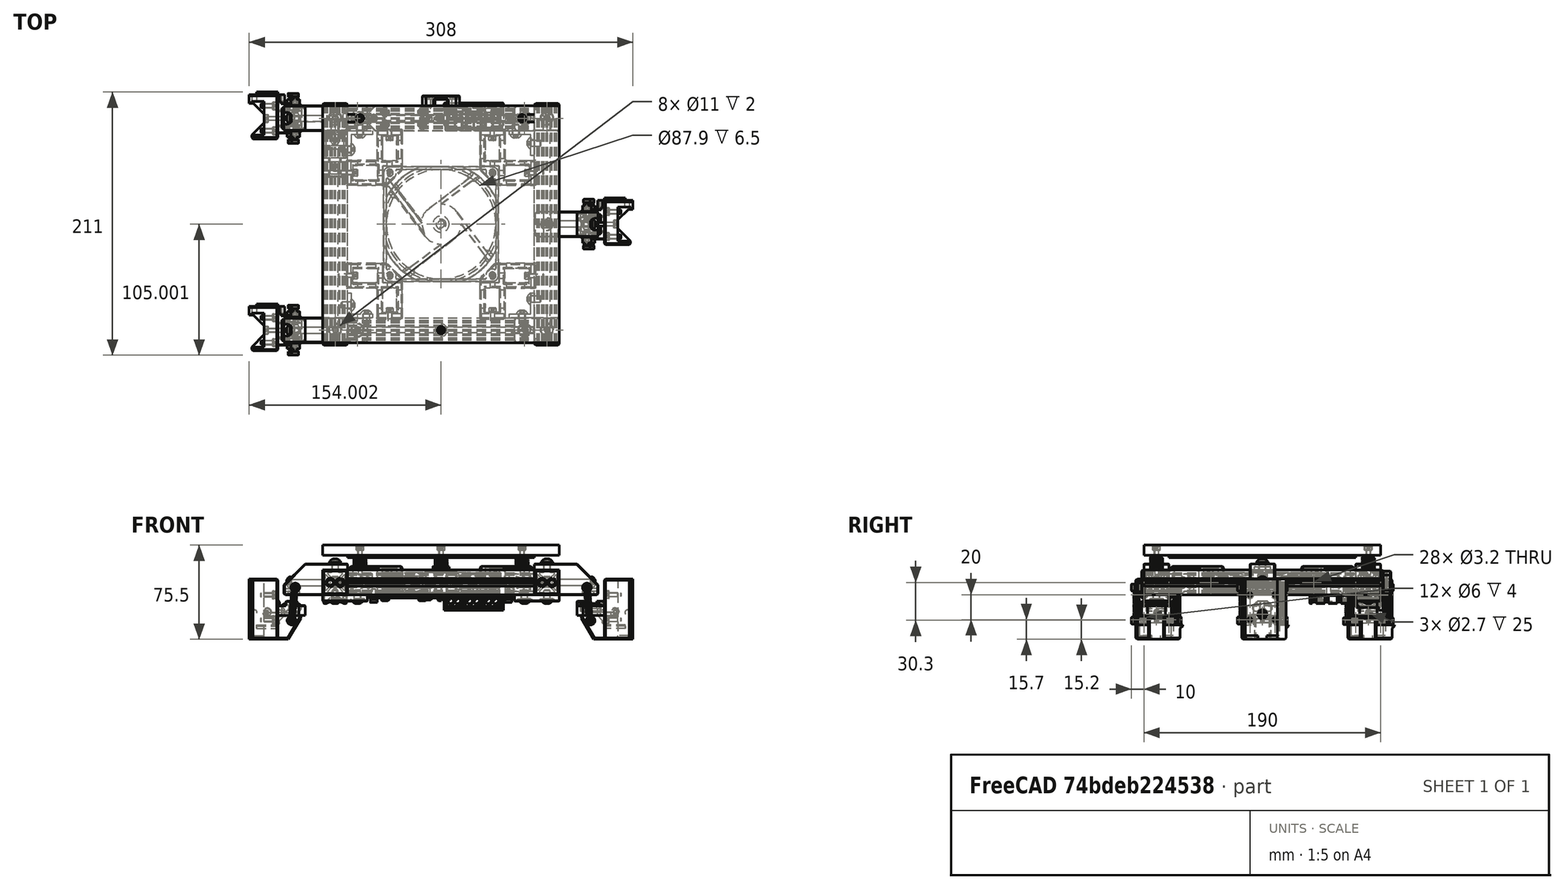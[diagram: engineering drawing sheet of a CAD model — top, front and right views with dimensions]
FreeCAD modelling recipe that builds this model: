
FCSTD DOCUMENT  (FreeCAD 0.19R24291 (Git))
Label: 180-bed-assembly
License: Other
LicenseURL: GPL3
objects: Part::FeaturePython×107, Part::Feature×58, App::Part×6, Part::Cylinder×6, Part::Sphere×3, Part::Box×1
note: 175 computed .brp shape members not serialized (recipe doc carries the construction recipe); baked Part::Feature solids carry a one-line shape summary decoded from their .brp

FEATURE [Part::Feature] Extrude003001  label="2020-190mm001"
  Placement = pos=(-85,-95,2.1e-14) rot=(-1,0,0;1.5708rad)
  shape: bbox 20 x 190 x 20 mm, 63 faces (baked)
FEATURE [Part::Feature] Extrude002  label="2020-150mm001"
  Placement = pos=(-75,-85,-1.7e-14) rot=(0,1,0;1.5708rad)
  shape: bbox 150 x 20 x 20 mm, 63 faces (baked)
FEATURE [Part::Feature] Extrude003002  label="2020-190mm002"
  Placement = pos=(85,-95,2.1e-14) rot=(-1,0,0;1.5708rad)
  shape: bbox 20 x 190 x 20 mm, 63 faces (baked)
FEATURE [Part::Feature] Extrude003003  label="2020-150mm002"
  Placement = pos=(-75,85,-1.7e-14) rot=(0,1,0;1.5708rad)
  shape: bbox 150 x 20 x 20 mm, 63 faces (baked)
FEATURE [Part::Box] Box001  label="150mm-heater-pad"
  AttacherType = Attacher::AttachEngine3D
  Height = 2
  Length = 150
  Placement = pos=(-75,-75,20) rot=(0,0,1;0rad)
  Width = 150
FEATURE [Part::Feature] AdditivePipe001  label="15mm-spring001"
  Placement = pos=(65,85,10) rot=(0,0,1;0rad)
  shape: bbox 10.45 x 11.2 x 10.36 mm, 42 faces (baked)
FEATURE [Part::Feature] AdditivePipe003  label="15mm-spring002"
  Placement = pos=(0,-85,10) rot=(0,0,1;0rad)
  shape: bbox 10.45 x 11.2 x 10.36 mm, 42 faces (baked)
FEATURE [Part::Feature] AdditivePipe005  label="15mm-spring003"
  Placement = pos=(-65,85,10) rot=(0,0,1;0rad)
  shape: bbox 10.45 x 11.2 x 10.36 mm, 42 faces (baked)
FEATURE [Part::Sphere] Sphere  label="8mm-ball-bearing"
  Angle1 = -90
  Angle2 = 90
  Angle3 = 360
  AttacherType = Attacher::AttachEngine3D
  Placement = pos=(0,0,4.9) rot=(0,0,1;0rad)
  Radius = 4
FEATURE [Part::Sphere] Sphere001  label="8mm-ball-bearing001"
  Angle1 = -90
  Angle2 = 90
  Angle3 = 360
  AttacherType = Attacher::AttachEngine3D
  Placement = pos=(0,0,4.9) rot=(0,0,1;0rad)
  Radius = 4
FEATURE [Part::Sphere] Sphere002  label="8mm-ball-bearing002"
  Angle1 = -90
  Angle2 = 90
  Angle3 = 360
  AttacherType = Attacher::AttachEngine3D
  Placement = pos=(0,0,4.9) rot=(0,0,1;0rad)
  Radius = 4
FEATURE [App::Part] Part005  label="bed-frame"
  Group = -> [Extrude003001,Extrude002,Extrude003002,Extrude003003]
  Origin = -> Origin005
FEATURE [Part::Feature] Cut010  label="190-aluminum-bed"
  shape: bbox 190 x 190 x 8 mm, 15 faces (baked)
FEATURE [Part::Feature] Cut007001  label="13x5.5x5-magnet003"
  shape: bbox 13 x 13 x 5 mm, 4 faces (baked)
FEATURE [App::Part] Part002  label="bed-magnet-slider002"
  Group = -> [Sphere002,Cut007001]
  Origin = -> Origin002
  Placement = pos=(-120,-85,-20) rot=(0,0,1;0rad)
FEATURE [Part::Feature] Cut003001  label="13x5.5x5-magnet004"
  shape: bbox 13 x 13 x 5 mm, 4 faces (baked)
FEATURE [App::Part] Part  label="bed-magnet-slider003"
  Group = -> [Sphere,Cut003001]
  Origin = -> Origin
  Placement = pos=(120,0,-20) rot=(0,0,1;1.5708rad)
FEATURE [Part::Feature] Cut006001  label="13x5.5x5-magnet005"
  shape: bbox 13 x 13 x 5 mm, 4 faces (baked)
FEATURE [App::Part] Part001  label="bed-magnet-slider001"
  Group = -> [Sphere001,Cut006001]
  Origin = -> Origin001
  Placement = pos=(-120,85,-20) rot=(0,0,1;0rad)
FEATURE [App::Part] Part006  label="bed-magnet"
  Group = -> [Part,Part001,Part002]
  Origin = -> Origin006
FEATURE [Part::Feature] Solid  label="2020-bracket"
  Placement = pos=(-75,-75,-1.7e-14) rot=(0,1,0;1.5708rad)
  shape: bbox 20 x 20 x 14 mm, 10 faces (baked)
FEATURE [Part::Feature] Solid001  label="2020-bracket001"
  Placement = pos=(75,-75,1.6e-14) rot=(0.57735,-0.57735,-0.57735;4.18879rad)
  shape: bbox 20 x 20 x 14 mm, 10 faces (baked)
FEATURE [Part::Feature] Solid002  label="2020-bracket002"
  Placement = pos=(75,75,1.6e-14) rot=(0.707107,0,-0.707107;3.14159rad)
  shape: bbox 20 x 20 x 14 mm, 10 faces (baked)
FEATURE [Part::Feature] Solid003  label="2020-bracket003"
  Placement = pos=(-75,75,-1.7e-14) rot=(0.57735,0.57735,-0.57735;2.0944rad)
  shape: bbox 20 x 20 x 14 mm, 10 faces (baked)
FEATURE [Part::FeaturePython] Screw  label="M5x8-Screw"  # Fasteners workbench fastener (typed FeaturePython)
  Placement = pos=(-72,-65,-1.6e-14) rot=(0,1,0;1.5708rad)
  baseObject = -> Solid [Edge1]
  diameter = 3
  invert = false
  length = 0
  lengthCustom = 8
  matchOuter = true
  offset = 0
  thread = false
  type = 39
FEATURE [Part::FeaturePython] Screw001  label="M5x8-Screw001"  # Fasteners workbench fastener (typed FeaturePython)
  Placement = pos=(-60,-72,-1.42e-14) rot=(-1,0,0;1.5708rad)
  baseObject = -> Solid [Edge13]
  diameter = 3
  invert = false
  length = 0
  lengthCustom = 8
  matchOuter = true
  offset = 0
  thread = false
  type = 39
FEATURE [Part::FeaturePython] Screw002  label="M5x8-Screw002"  # Fasteners workbench fastener (typed FeaturePython)
  Placement = pos=(65,-72,1.4e-14) rot=(-1,0,0;1.5708rad)
  baseObject = -> Solid001 [Edge1]
  diameter = 3
  invert = false
  length = 0
  lengthCustom = 8
  matchOuter = true
  offset = 0
  thread = false
  type = 39
FEATURE [Part::FeaturePython] Screw003  label="M5x8-Screw003"  # Fasteners workbench fastener (typed FeaturePython)
  Placement = pos=(72,-60,1.5e-14) rot=(0,-1,0;1.5708rad)
  baseObject = -> Solid001 [Edge13]
  diameter = 3
  invert = false
  length = 0
  lengthCustom = 8
  matchOuter = true
  offset = 0
  thread = false
  type = 39
FEATURE [Part::FeaturePython] Screw004  label="M5x8-Screw004"  # Fasteners workbench fastener (typed FeaturePython)
  Placement = pos=(72,65,1.7e-14) rot=(0,-1,0;1.5708rad)
  baseObject = -> Solid002 [Edge1]
  diameter = 3
  invert = false
  length = 0
  lengthCustom = 8
  matchOuter = true
  offset = 0
  thread = false
  type = 39
FEATURE [Part::FeaturePython] Screw005  label="M5x8-Screw005"  # Fasteners workbench fastener (typed FeaturePython)
  Placement = pos=(60,72,1.8e-14) rot=(1,0,0;1.5708rad)
  baseObject = -> Solid002 [Edge13]
  diameter = 3
  invert = false
  length = 0
  lengthCustom = 8
  matchOuter = true
  offset = 0
  thread = false
  type = 39
FEATURE [Part::FeaturePython] Screw006  label="M5x8-Screw006"  # Fasteners workbench fastener (typed FeaturePython)
  Placement = pos=(-72,60,-1.8e-14) rot=(0,1,0;1.5708rad)
  baseObject = -> Solid003 [Edge13]
  diameter = 3
  invert = false
  length = 0
  lengthCustom = 8
  matchOuter = true
  offset = 0
  thread = false
  type = 39
FEATURE [Part::FeaturePython] Screw007  label="M5x8-Screw007"  # Fasteners workbench fastener (typed FeaturePython)
  Placement = pos=(-65,72,-1.5e-14) rot=(1,0,0;1.5708rad)
  baseObject = -> Solid003 [Edge1]
  diameter = 3
  invert = false
  length = 0
  lengthCustom = 8
  matchOuter = true
  offset = 0
  thread = false
  type = 39
FEATURE [Part::FeaturePython] Screw011  label="M3x20-Screw"  # Fasteners workbench fastener (typed FeaturePython)
  Placement = pos=(0,-85,26) rot=(0,0,1;0rad)
  baseObject = -> Cut010 [Edge25]
  diameter = 4
  invert = false
  length = 10
  lengthCustom = 20
  matchOuter = true
  offset = 0
  thread = false
  type = 33
FEATURE [Part::FeaturePython] Screw012  label="M3x20-Screw001"  # Fasteners workbench fastener (typed FeaturePython)
  Placement = pos=(65,85,26) rot=(0,0,1;0rad)
  baseObject = -> Cut010 [Edge29]
  diameter = 4
  invert = false
  length = 10
  lengthCustom = 20
  matchOuter = true
  offset = 0
  thread = false
  type = 33
FEATURE [Part::FeaturePython] Screw013  label="M3x20-Screw002"  # Fasteners workbench fastener (typed FeaturePython)
  Placement = pos=(-65,85,26) rot=(0,0,1;0rad)
  baseObject = -> Cut010 [Edge27]
  diameter = 4
  invert = false
  length = 10
  lengthCustom = 20
  matchOuter = true
  offset = 0
  thread = false
  type = 33
FEATURE [Part::FeaturePython] Washer010  label="M3-Washer"  # Fasteners workbench fastener (typed FeaturePython)
  Placement = pos=(-135,-95,-29.8) rot=(0,1,0;1.5708rad)
  diameter = 4
  invert = false
  matchOuter = true
  offset = 0
  type = 5
FEATURE [Part::FeaturePython] Washer011  label="M3-Washer042"  # Fasteners workbench fastener (typed FeaturePython)
  Placement = pos=(-135,-95,-9.8) rot=(0,1,0;1.5708rad)
  diameter = 4
  invert = false
  matchOuter = true
  offset = 0
  type = 5
FEATURE [Part::FeaturePython] Washer012  label="M3-Washer043"  # Fasteners workbench fastener (typed FeaturePython)
  Placement = pos=(-135,-75,-9.8) rot=(0,1,0;1.5708rad)
  diameter = 4
  invert = false
  matchOuter = true
  offset = 0
  type = 5
FEATURE [Part::FeaturePython] Washer013  label="M3-Washer041"  # Fasteners workbench fastener (typed FeaturePython)
  Placement = pos=(-135,-75,-29.8) rot=(0,1,0;1.5708rad)
  diameter = 4
  invert = false
  matchOuter = true
  offset = 0
  type = 5
FEATURE [Part::FeaturePython] Washer014  label="M3-Washer046"  # Fasteners workbench fastener (typed FeaturePython)
  Placement = pos=(-135,75,-30.3) rot=(0,1,0;1.5708rad)
  diameter = 4
  invert = false
  matchOuter = true
  offset = 0
  type = 5
FEATURE [Part::FeaturePython] Washer015  label="M3-Washer047"  # Fasteners workbench fastener (typed FeaturePython)
  Placement = pos=(-135,75,-10.3) rot=(0,1,0;1.5708rad)
  diameter = 4
  invert = false
  matchOuter = true
  offset = 0
  type = 5
FEATURE [Part::FeaturePython] Washer016  label="M3-Washer045"  # Fasteners workbench fastener (typed FeaturePython)
  Placement = pos=(-135,95,-10.3) rot=(0,1,0;1.5708rad)
  diameter = 4
  invert = false
  matchOuter = true
  offset = 0
  type = 5
FEATURE [Part::FeaturePython] Washer017  label="M3-Washer044"  # Fasteners workbench fastener (typed FeaturePython)
  Placement = pos=(-135,95,-30.3) rot=(0,1,0;1.5708rad)
  diameter = 4
  invert = false
  matchOuter = true
  offset = 0
  type = 5
FEATURE [Part::FeaturePython] Screw034  label="M3x10-Screw044"  # Fasteners workbench fastener (typed FeaturePython)
  Placement = pos=(-134.45,75,-10.3) rot=(0,1,0;1.5708rad)
  baseObject = -> Washer015 [Edge1]
  diameter = 4
  invert = false
  length = 3
  lengthCustom = 10
  matchOuter = true
  offset = 0
  thread = false
  type = 33
FEATURE [Part::FeaturePython] Screw035  label="M3x10-Screw043"  # Fasteners workbench fastener (typed FeaturePython)
  Placement = pos=(-134.45,95,-10.3) rot=(0,1,0;1.5708rad)
  baseObject = -> Washer016 [Edge1]
  diameter = 4
  invert = false
  length = 3
  lengthCustom = 10
  matchOuter = true
  offset = 0
  thread = false
  type = 33
FEATURE [Part::FeaturePython] Screw036  label="M3x10-Screw042"  # Fasteners workbench fastener (typed FeaturePython)
  Placement = pos=(-134.45,95,-30.3) rot=(0,1,0;1.5708rad)
  baseObject = -> Washer017 [Edge1]
  diameter = 4
  invert = false
  length = 3
  lengthCustom = 10
  matchOuter = true
  offset = 0
  thread = false
  type = 33
FEATURE [Part::FeaturePython] Screw037  label="M3x10-Screw041"  # Fasteners workbench fastener (typed FeaturePython)
  Placement = pos=(-134.45,75,-30.3) rot=(0,1,0;1.5708rad)
  baseObject = -> Washer014 [Edge1]
  diameter = 4
  invert = false
  length = 3
  lengthCustom = 10
  matchOuter = true
  offset = 0
  thread = false
  type = 33
FEATURE [Part::FeaturePython] Screw039  label="M3x10-Screw038"  # Fasteners workbench fastener (typed FeaturePython)
  Placement = pos=(-134.45,-95,-29.8) rot=(0,1,0;1.5708rad)
  baseObject = -> Washer010 [Edge1]
  diameter = 4
  invert = false
  length = 3
  lengthCustom = 10
  matchOuter = true
  offset = 0
  thread = false
  type = 33
FEATURE [Part::FeaturePython] Screw040  label="M3x10-Screw037"  # Fasteners workbench fastener (typed FeaturePython)
  Placement = pos=(-134.45,-75,-29.8) rot=(0,1,0;1.5708rad)
  baseObject = -> Washer013 [Edge1]
  diameter = 4
  invert = false
  length = 3
  lengthCustom = 10
  matchOuter = true
  offset = 0
  thread = false
  type = 33
FEATURE [Part::FeaturePython] Screw041  label="M3x10-Screw040"  # Fasteners workbench fastener (typed FeaturePython)
  Placement = pos=(-134.45,-75,-9.8) rot=(0,1,0;1.5708rad)
  baseObject = -> Washer012 [Edge1]
  diameter = 4
  invert = false
  length = 3
  lengthCustom = 10
  matchOuter = true
  offset = 0
  thread = false
  type = 33
FEATURE [Part::FeaturePython] Screw042  label="M3x10-Screw039"  # Fasteners workbench fastener (typed FeaturePython)
  Placement = pos=(-134.45,-95,-9.8) rot=(0,1,0;1.5708rad)
  baseObject = -> Washer011 [Edge1]
  diameter = 4
  invert = false
  length = 3
  lengthCustom = 10
  matchOuter = true
  offset = 0
  thread = false
  type = 33
FEATURE [Part::FeaturePython] Washer018  label="M3-Washer049"  # Fasteners workbench fastener (typed FeaturePython)
  Placement = pos=(135,10,-9.8) rot=(0,-1,0;1.5708rad)
  diameter = 4
  invert = true
  matchOuter = true
  offset = 0
  type = 5
FEATURE [Part::FeaturePython] Washer019  label="M3-Washer050"  # Fasteners workbench fastener (typed FeaturePython)
  Placement = pos=(135,10,-29.8) rot=(0,-1,0;1.5708rad)
  diameter = 4
  invert = true
  matchOuter = true
  offset = 0
  type = 5
FEATURE [Part::FeaturePython] Washer020  label="M3-Washer048"  # Fasteners workbench fastener (typed FeaturePython)
  Placement = pos=(135,-10,-9.8) rot=(0,-1,0;1.5708rad)
  diameter = 4
  invert = true
  matchOuter = true
  offset = 0
  type = 5
FEATURE [Part::FeaturePython] Washer021  label="M3-Washer051"  # Fasteners workbench fastener (typed FeaturePython)
  Placement = pos=(135,-10,-29.8) rot=(0,-1,0;1.5708rad)
  diameter = 4
  invert = true
  matchOuter = true
  offset = 0
  type = 5
FEATURE [Part::FeaturePython] Screw043  label="M3x10-Screw046"  # Fasteners workbench fastener (typed FeaturePython)
  Placement = pos=(134.45,10,-29.8) rot=(0,-1,0;1.5708rad)
  baseObject = -> Washer019 [Edge1]
  diameter = 4
  invert = false
  length = 10
  lengthCustom = 10
  matchOuter = true
  offset = 0
  thread = false
  type = 33
FEATURE [Part::FeaturePython] Screw044  label="M3x10-Screw047"  # Fasteners workbench fastener (typed FeaturePython)
  Placement = pos=(134.45,-10,-29.8) rot=(0,-1,0;1.5708rad)
  baseObject = -> Washer021 [Edge1]
  diameter = 4
  invert = false
  length = 10
  lengthCustom = 10
  matchOuter = true
  offset = 0
  thread = false
  type = 33
FEATURE [Part::FeaturePython] Screw045  label="M3x10-Screw048"  # Fasteners workbench fastener (typed FeaturePython)
  Placement = pos=(134.45,-10,-9.8) rot=(0,-1,0;1.5708rad)
  baseObject = -> Washer020 [Edge1]
  diameter = 4
  invert = false
  length = 10
  lengthCustom = 10
  matchOuter = true
  offset = 0
  thread = false
  type = 33
FEATURE [Part::FeaturePython] Screw046  label="M3x10-Screw045"  # Fasteners workbench fastener (typed FeaturePython)
  Placement = pos=(134.45,10,-9.8) rot=(0,-1,0;1.5708rad)
  baseObject = -> Washer018 [Edge1]
  diameter = 4
  invert = false
  length = 10
  lengthCustom = 10
  matchOuter = true
  offset = 0
  thread = false
  type = 33
FEATURE [Part::Feature] Chamfer004013007011015006009007001002  label="bed-frame-mount-top005"
  Placement = pos=(-142,85,-45) rot=(0,0,1;0rad)
  shape: bbox 51 x 20 x 25 mm, 56 faces (baked)
FEATURE [Part::Feature] Chamfer004013007011015006009007001003  label="bed-frame-mount-top006"
  Placement = pos=(142,-2.9e-14,-45) rot=(0,0,1;3.14159rad)
  shape: bbox 51 x 20 x 25 mm, 56 faces (baked)
FEATURE [Part::Feature] Chamfer004013007011015006009007001001  label="bed-frame-mount-top004"
  Placement = pos=(-142,-85,-45) rot=(0,0,1;0rad)
  shape: bbox 51 x 20 x 25 mm, 56 faces (baked)
FEATURE [Part::FeaturePython] Screw047  label="M3x12-Screw015"  # Fasteners workbench fastener (typed FeaturePython)
  Placement = pos=(-117,102,-4) rot=(-1,0,0;1.5708rad)
  baseObject = -> Chamfer004013007011015006009007001002 [Edge138]
  diameter = 4
  invert = true
  length = 4
  lengthCustom = 12
  matchOuter = false
  offset = 7
  thread = false
  type = 33
FEATURE [Part::FeaturePython] Screw048  label="M3x12-Screw014"  # Fasteners workbench fastener (typed FeaturePython)
  Placement = pos=(-117,68,-4) rot=(1,0,0;1.5708rad)
  baseObject = -> Chamfer004013007011015006009007001002 [Edge132]
  diameter = 4
  invert = false
  length = 4
  lengthCustom = 12
  matchOuter = false
  offset = 7
  thread = false
  type = 33
FEATURE [Part::FeaturePython] Screw049  label="M3x12-Screw017"  # Fasteners workbench fastener (typed FeaturePython)
  Placement = pos=(-117,-68,-4) rot=(-1,0,0;1.5708rad)
  baseObject = -> Chamfer004013007011015006009007001001 [Edge138]
  diameter = 4
  invert = true
  length = 4
  lengthCustom = 12
  matchOuter = false
  offset = 7
  thread = false
  type = 33
FEATURE [Part::FeaturePython] Screw050  label="M3x12-Screw016"  # Fasteners workbench fastener (typed FeaturePython)
  Placement = pos=(-117,-102,-4) rot=(1,0,0;1.5708rad)
  baseObject = -> Chamfer004013007011015006009007001001 [Edge132]
  diameter = 4
  invert = false
  length = 4
  lengthCustom = 12
  matchOuter = false
  offset = 7
  thread = false
  type = 33
FEATURE [Part::FeaturePython] Screw051  label="M3x12-Screw009"  # Fasteners workbench fastener (typed FeaturePython)
  Placement = pos=(117,-17,-4) rot=(1,0,0;1.5708rad)
  baseObject = -> Chamfer004013007011015006009007001003 [Edge138]
  diameter = 4
  invert = true
  length = 4
  lengthCustom = 12
  matchOuter = true
  offset = 7
  thread = false
  type = 33
FEATURE [Part::FeaturePython] Screw052  label="M3x12-Screw008"  # Fasteners workbench fastener (typed FeaturePython)
  Placement = pos=(117,17,-4) rot=(-1,0,0;1.5708rad)
  baseObject = -> Chamfer004013007011015006009007001003 [Edge132]
  diameter = 4
  invert = false
  length = 4
  lengthCustom = 12
  matchOuter = true
  offset = 7
  thread = false
  type = 33
FEATURE [Part::FeaturePython] Washer  label="M5-Washer"  # Fasteners workbench fastener (typed FeaturePython)
  Placement = pos=(-85,85,15) rot=(0,0,1;0rad)
  baseObject = -> Chamfer004013007011015006009007001002 [Edge58]
  diameter = 1
  invert = false
  matchOuter = true
  offset = 0
  type = 4
FEATURE [Part::FeaturePython] Washer022  label="M5-Washer001"  # Fasteners workbench fastener (typed FeaturePython)
  Placement = pos=(-85,-85,15) rot=(0,0,1;0rad)
  baseObject = -> Chamfer004013007011015006009007001001 [Edge58]
  diameter = 1
  invert = false
  matchOuter = true
  offset = 0
  type = 4
FEATURE [Part::FeaturePython] Washer023  label="M5-Washer002"  # Fasteners workbench fastener (typed FeaturePython)
  Placement = pos=(85,-2.19e-14,15) rot=(0,0,1;0rad)
  baseObject = -> Chamfer004013007011015006009007001003 [Edge58]
  diameter = 1
  invert = false
  matchOuter = true
  offset = 0
  type = 4
FEATURE [Part::FeaturePython] Screw053  label="M5x12-Screw"  # Fasteners workbench fastener (typed FeaturePython)
  Placement = pos=(-85,85,16.1) rot=(0,0,1;0rad)
  baseObject = -> Washer [Edge1]
  diameter = 3
  invert = false
  length = 2
  lengthCustom = 12
  matchOuter = true
  offset = 0
  thread = false
  type = 39
FEATURE [Part::FeaturePython] Screw054  label="M5x12-Screw001"  # Fasteners workbench fastener (typed FeaturePython)
  Placement = pos=(-85,-85,16.1) rot=(0,0,1;0rad)
  baseObject = -> Washer022 [Edge1]
  diameter = 3
  invert = false
  length = 2
  lengthCustom = 12
  matchOuter = true
  offset = 0
  thread = false
  type = 39
FEATURE [Part::FeaturePython] Screw055  label="M5x12-Screw002"  # Fasteners workbench fastener (typed FeaturePython)
  Placement = pos=(85,-2.19e-14,16.1) rot=(0,0,1;0rad)
  baseObject = -> Washer023 [Edge1]
  diameter = 3
  invert = false
  length = 2
  lengthCustom = 12
  matchOuter = true
  offset = 0
  thread = false
  type = 39
FEATURE [Part::FeaturePython] Washer024  label="M5-Washer006"  # Fasteners workbench fastener (typed FeaturePython)
  Placement = pos=(-120,85,0) rot=(0,-1,0;1.5708rad)
  baseObject = -> Chamfer004013007011015006009007001002 [Edge86]
  diameter = 6
  invert = true
  matchOuter = true
  offset = 0
  type = 5
FEATURE [Part::FeaturePython] Washer025  label="M5-Washer007"  # Fasteners workbench fastener (typed FeaturePython)
  Placement = pos=(-120,-85,0) rot=(0,-1,0;1.5708rad)
  baseObject = -> Chamfer004013007011015006009007001001 [Edge86]
  diameter = 6
  invert = true
  matchOuter = true
  offset = 0
  type = 5
FEATURE [Part::FeaturePython] Washer026  label="M5-Washer005"  # Fasteners workbench fastener (typed FeaturePython)
  Placement = pos=(120,-2.6e-14,0) rot=(0,1,0;1.5708rad)
  baseObject = -> Chamfer004013007011015006009007001003 [Edge86]
  diameter = 6
  invert = true
  matchOuter = true
  offset = 0
  type = 5
FEATURE [Part::FeaturePython] Screw056  label="M5x30-Screw"  # Fasteners workbench fastener (typed FeaturePython)
  Placement = pos=(-121.1,85,0) rot=(0,-1,0;1.5708rad)
  baseObject = -> Washer024 [Edge1]
  diameter = 3
  invert = false
  length = 7
  lengthCustom = 30
  matchOuter = true
  offset = 0
  thread = false
  type = 39
FEATURE [Part::FeaturePython] Screw057  label="M5x30-Screw001"  # Fasteners workbench fastener (typed FeaturePython)
  Placement = pos=(-121.1,-85,0) rot=(0,-1,0;1.5708rad)
  baseObject = -> Washer025 [Edge1]
  diameter = 3
  invert = false
  length = 7
  lengthCustom = 30
  matchOuter = true
  offset = 0
  thread = false
  type = 39
FEATURE [Part::FeaturePython] Screw058  label="M5x30-Screw002"  # Fasteners workbench fastener (typed FeaturePython)
  Placement = pos=(121.1,-2.6e-14,0) rot=(0,1,0;1.5708rad)
  baseObject = -> Washer026 [Edge1]
  diameter = 3
  invert = false
  length = 7
  lengthCustom = 30
  matchOuter = true
  offset = 0
  thread = false
  type = 39
FEATURE [Part::FeaturePython] Screw059  label="M3x16-Screw007"  # Fasteners workbench fastener (typed FeaturePython)
  Placement = pos=(-120,-102,-30.5) rot=(1,0,0;1.5708rad)
  diameter = 4
  invert = false
  length = 6
  lengthCustom = 16
  matchOuter = true
  offset = 6.5
  thread = false
  type = 33
FEATURE [Part::FeaturePython] Screw060  label="M3x16-Screw"  # Fasteners workbench fastener (typed FeaturePython)
  Placement = pos=(-120,-68,-30.5) rot=(-1,0,0;1.5708rad)
  diameter = 4
  invert = true
  length = 6
  lengthCustom = 16
  matchOuter = true
  offset = 6.5
  thread = false
  type = 33
FEATURE [Part::FeaturePython] Screw061  label="M3x16-Screw009"  # Fasteners workbench fastener (typed FeaturePython)
  Placement = pos=(-120,102,-31) rot=(-1,0,0;1.5708rad)
  diameter = 4
  invert = true
  length = 6
  lengthCustom = 16
  matchOuter = true
  offset = 6.5
  thread = false
  type = 33
FEATURE [Part::FeaturePython] Screw062  label="M3x16-Screw008"  # Fasteners workbench fastener (typed FeaturePython)
  Placement = pos=(-120,68,-31) rot=(1,0,0;1.5708rad)
  diameter = 4
  invert = false
  length = 6
  lengthCustom = 16
  matchOuter = true
  offset = 6.5
  thread = false
  type = 33
FEATURE [Part::FeaturePython] Screw063  label="M3x16-Screw005"  # Fasteners workbench fastener (typed FeaturePython)
  Placement = pos=(120,-17,-30.5) rot=(1,0,0;1.5708rad)
  diameter = 4
  invert = true
  length = 6
  lengthCustom = 16
  matchOuter = true
  offset = 6.5
  thread = false
  type = 33
FEATURE [Part::FeaturePython] Screw064  label="M3x16-Screw006"  # Fasteners workbench fastener (typed FeaturePython)
  Placement = pos=(120,17,-30.5) rot=(-1,0,0;1.5708rad)
  diameter = 4
  invert = false
  length = 6
  lengthCustom = 16
  matchOuter = true
  offset = 6.5
  thread = false
  type = 33
FEATURE [Part::Feature] Chamfer001
  Placement = pos=(-95,-95,-15) rot=(0,0,1;0rad)
  shape: bbox 36 x 20 x 6 mm, 35 faces (baked)
FEATURE [Part::Feature] Chamfer004013007011015006009007001005
  Placement = pos=(95,95,-15) rot=(0,0,1;3.14159rad)
  shape: bbox 36 x 20 x 6 mm, 35 faces (baked)
FEATURE [Part::Feature] Chamfer004013007011015006009007001006
  Placement = pos=(95,-75,-15) rot=(0,0,1;3.14159rad)
  shape: bbox 36 x 20 x 6 mm, 35 faces (baked)
FEATURE [Part::FeaturePython] Washer027  label="M5-Washer016"  # Fasteners workbench fastener (typed FeaturePython)
  Placement = pos=(-85,-85,-13) rot=(1,0,0;3.14159rad)
  baseObject = -> Chamfer001 [Edge75]
  diameter = 1
  invert = true
  matchOuter = true
  offset = 0
  type = 4
FEATURE [Part::FeaturePython] Washer028  label="M5-Washer017"  # Fasteners workbench fastener (typed FeaturePython)
  Placement = pos=(-67,-85,-13) rot=(1,0,0;3.14159rad)
  baseObject = -> Chamfer001 [Edge74]
  diameter = 1
  invert = true
  matchOuter = true
  offset = 0
  type = 4
FEATURE [Part::FeaturePython] Washer029  label="M5-Washer025"  # Fasteners workbench fastener (typed FeaturePython)
  Placement = pos=(-85,85,-13) rot=(1,0,0;3.14159rad)
  diameter = 1
  invert = true
  matchOuter = true
  offset = 0
  type = 4
FEATURE [Part::FeaturePython] Washer030  label="M5-Washer024"  # Fasteners workbench fastener (typed FeaturePython)
  Placement = pos=(-67,85,-13) rot=(1,0,0;3.14159rad)
  diameter = 1
  invert = true
  matchOuter = true
  offset = 0
  type = 4
FEATURE [Part::FeaturePython] Washer031  label="M5-Washer020"  # Fasteners workbench fastener (typed FeaturePython)
  Placement = pos=(67,85,-13) rot=(1,0,0;3.14159rad)
  baseObject = -> Chamfer004013007011015006009007001005 [Edge74]
  diameter = 1
  invert = true
  matchOuter = true
  offset = 0
  type = 4
FEATURE [Part::FeaturePython] Washer032  label="M5-Washer021"  # Fasteners workbench fastener (typed FeaturePython)
  Placement = pos=(85,85,-13) rot=(1,0,0;3.14159rad)
  baseObject = -> Chamfer004013007011015006009007001005 [Edge75]
  diameter = 1
  invert = true
  matchOuter = true
  offset = 0
  type = 4
FEATURE [Part::FeaturePython] Washer033  label="M5-Washer022"  # Fasteners workbench fastener (typed FeaturePython)
  Placement = pos=(67,-85,-13) rot=(1,0,0;3.14159rad)
  baseObject = -> Chamfer004013007011015006009007001006 [Edge74]
  diameter = 1
  invert = true
  matchOuter = true
  offset = 0
  type = 4
FEATURE [Part::FeaturePython] Washer034  label="M5-Washer023"  # Fasteners workbench fastener (typed FeaturePython)
  Placement = pos=(85,-85,-13) rot=(1,0,0;3.14159rad)
  baseObject = -> Chamfer004013007011015006009007001006 [Edge75]
  diameter = 1
  invert = true
  matchOuter = true
  offset = 0
  type = 4
FEATURE [Part::FeaturePython] Screw065  label="M5x8-Screw008"  # Fasteners workbench fastener (typed FeaturePython)
  Placement = pos=(-85,-85,-14.1) rot=(1,0,0;3.14159rad)
  baseObject = -> Washer027 [Edge1]
  diameter = 3
  invert = false
  length = 0
  lengthCustom = 8
  matchOuter = true
  offset = 0
  thread = false
  type = 39
FEATURE [Part::FeaturePython] Screw066  label="M5x8-Screw009"  # Fasteners workbench fastener (typed FeaturePython)
  Placement = pos=(-67,-85,-14.1) rot=(1,0,0;3.14159rad)
  baseObject = -> Washer028 [Edge1]
  diameter = 3
  invert = false
  length = 0
  lengthCustom = 8
  matchOuter = true
  offset = 0
  thread = false
  type = 39
FEATURE [Part::FeaturePython] Screw067  label="M5x8-Screw017"  # Fasteners workbench fastener (typed FeaturePython)
  Placement = pos=(-85,85,-14.1) rot=(1,0,0;3.14159rad)
  baseObject = -> Washer029 [Edge1]
  diameter = 3
  invert = false
  length = 0
  lengthCustom = 8
  matchOuter = true
  offset = 0
  thread = false
  type = 39
FEATURE [Part::FeaturePython] Screw068  label="M5x8-Screw016"  # Fasteners workbench fastener (typed FeaturePython)
  Placement = pos=(-67,85,-14.1) rot=(1,0,0;3.14159rad)
  baseObject = -> Washer030 [Edge1]
  diameter = 3
  invert = false
  length = 0
  lengthCustom = 8
  matchOuter = true
  offset = 0
  thread = false
  type = 39
FEATURE [Part::FeaturePython] Screw069  label="M5x8-Screw012"  # Fasteners workbench fastener (typed FeaturePython)
  Placement = pos=(67,85,-14.1) rot=(1,0,0;3.14159rad)
  baseObject = -> Washer031 [Edge1]
  diameter = 3
  invert = false
  length = 0
  lengthCustom = 8
  matchOuter = true
  offset = 0
  thread = false
  type = 39
FEATURE [Part::FeaturePython] Screw070  label="M5x8-Screw013"  # Fasteners workbench fastener (typed FeaturePython)
  Placement = pos=(85,85,-14.1) rot=(1,0,0;3.14159rad)
  baseObject = -> Washer032 [Edge1]
  diameter = 3
  invert = false
  length = 0
  lengthCustom = 8
  matchOuter = true
  offset = 0
  thread = false
  type = 39
FEATURE [Part::FeaturePython] Screw071  label="M5x8-Screw014"  # Fasteners workbench fastener (typed FeaturePython)
  Placement = pos=(67,-85,-14.1) rot=(1,0,0;3.14159rad)
  baseObject = -> Washer033 [Edge1]
  diameter = 3
  invert = false
  length = 0
  lengthCustom = 8
  matchOuter = true
  offset = 0
  thread = false
  type = 39
FEATURE [Part::FeaturePython] Screw072  label="M5x8-Screw015"  # Fasteners workbench fastener (typed FeaturePython)
  Placement = pos=(85,-85,-14.1) rot=(1,0,0;3.14159rad)
  baseObject = -> Washer034 [Edge1]
  diameter = 3
  invert = false
  length = 0
  lengthCustom = 8
  matchOuter = true
  offset = 0
  thread = false
  type = 39
FEATURE [Part::Feature] Fillet001001  label="92mm-fan-mounter"
  Placement = pos=(41.25,41.25,10) rot=(0,1,0;3.14159rad)
  shape: bbox 44.75 x 44.75 x 23 mm, 72 faces (baked)
FEATURE [Part::Feature] Fillet001002  label="92mm-fan-mounter001"
  Placement = pos=(-41.25,41.25,10) rot=(0.707107,-0.707107,0;3.14159rad)
  shape: bbox 44.75 x 44.75 x 23 mm, 72 faces (baked)
FEATURE [Part::Feature] Fillet001003  label="92mm-fan-mounter002"
  Placement = pos=(-41.25,-41.25,10) rot=(1,0,0;3.14159rad)
  shape: bbox 44.75 x 44.75 x 23 mm, 72 faces (baked)
FEATURE [Part::Feature] Fillet001004  label="92mm-fan-mounter003"
  Placement = pos=(41.25,-41.25,10) rot=(0.707107,0.707107,0;3.14159rad)
  shape: bbox 44.75 x 44.75 x 23 mm, 72 faces (baked)
FEATURE [Part::Feature] Fusion001001  label="92mm-slim0fan"
  Placement = pos=(0,2e-15,8) rot=(1,0,0;3.14159rad)
  shape: bbox 118.8 x 118.8 x 17.52 mm, 159 faces (baked)
FEATURE [Part::FeaturePython] Washer035  label="M3-Washer060"  # Fasteners workbench fastener (typed FeaturePython)
  Placement = pos=(70.75,-41.25,5e-15) rot=(0,-1,0;1.5708rad)
  baseObject = -> Fillet001004 [Edge178]
  diameter = 4
  invert = true
  matchOuter = true
  offset = 0
  type = 5
FEATURE [Part::FeaturePython] Washer036  label="M3-Washer061"  # Fasteners workbench fastener (typed FeaturePython)
  Placement = pos=(41.25,-70.75,5e-15) rot=(-1,0,0;1.5708rad)
  baseObject = -> Fillet001004 [Edge190]
  diameter = 4
  invert = true
  matchOuter = true
  offset = 0
  type = 5
FEATURE [Part::FeaturePython] Washer037  label="M3-Washer062"  # Fasteners workbench fastener (typed FeaturePython)
  Placement = pos=(41.25,70.75,1.1e-14) rot=(1,0,0;1.5708rad)
  baseObject = -> Fillet001001 [Edge178]
  diameter = 4
  invert = true
  matchOuter = true
  offset = 0
  type = 5
FEATURE [Part::FeaturePython] Washer038  label="M3-Washer063"  # Fasteners workbench fastener (typed FeaturePython)
  Placement = pos=(70.75,41.25,1.4e-14) rot=(0,-1,0;1.5708rad)
  baseObject = -> Fillet001001 [Edge190]
  diameter = 4
  invert = true
  matchOuter = true
  offset = 0
  type = 5
FEATURE [Part::FeaturePython] Washer039  label="M3-Washer064"  # Fasteners workbench fastener (typed FeaturePython)
  Placement = pos=(-70.75,41.25,5e-15) rot=(0,1,0;1.5708rad)
  baseObject = -> Fillet001002 [Edge178]
  diameter = 4
  invert = true
  matchOuter = true
  offset = 0
  type = 5
FEATURE [Part::FeaturePython] Washer040  label="M3-Washer065"  # Fasteners workbench fastener (typed FeaturePython)
  Placement = pos=(-41.25,70.75,5e-15) rot=(1,0,0;1.5708rad)
  baseObject = -> Fillet001002 [Edge190]
  diameter = 4
  invert = true
  matchOuter = true
  offset = 0
  type = 5
FEATURE [Part::FeaturePython] Washer041  label="M3-Washer066"  # Fasteners workbench fastener (typed FeaturePython)
  Placement = pos=(-41.25,-70.75,5e-15) rot=(-1,0,0;1.5708rad)
  baseObject = -> Fillet001003 [Edge178]
  diameter = 4
  invert = true
  matchOuter = true
  offset = 0
  type = 5
FEATURE [Part::FeaturePython] Washer042  label="M3-Washer067"  # Fasteners workbench fastener (typed FeaturePython)
  Placement = pos=(-70.75,-41.25,5e-15) rot=(0,1,0;1.5708rad)
  baseObject = -> Fillet001003 [Edge190]
  diameter = 4
  invert = true
  matchOuter = true
  offset = 0
  type = 5
FEATURE [Part::FeaturePython] Screw073  label="M3x12-Screw"  # Fasteners workbench fastener (typed FeaturePython)
  Placement = pos=(-70.2,41.25,5e-15) rot=(0,1,0;1.5708rad)
  baseObject = -> Washer039 [Edge1]
  diameter = 4
  invert = false
  length = 4
  lengthCustom = 12
  matchOuter = true
  offset = 0
  thread = false
  type = 33
FEATURE [Part::FeaturePython] Screw074  label="M3x12-Screw001"  # Fasteners workbench fastener (typed FeaturePython)
  Placement = pos=(-41.25,70.2,5e-15) rot=(1,0,0;1.5708rad)
  baseObject = -> Washer040 [Edge1]
  diameter = 4
  invert = false
  length = 4
  lengthCustom = 12
  matchOuter = true
  offset = 0
  thread = false
  type = 33
FEATURE [Part::FeaturePython] Screw075  label="M3x12-Screw002"  # Fasteners workbench fastener (typed FeaturePython)
  Placement = pos=(70.2,41.25,1.4e-14) rot=(0,-1,0;1.5708rad)
  baseObject = -> Washer038 [Edge1]
  diameter = 4
  invert = false
  length = 4
  lengthCustom = 12
  matchOuter = true
  offset = 0
  thread = false
  type = 33
FEATURE [Part::FeaturePython] Screw076  label="M3x12-Screw003"  # Fasteners workbench fastener (typed FeaturePython)
  Placement = pos=(41.25,70.2,1.1e-14) rot=(1,0,0;1.5708rad)
  baseObject = -> Washer037 [Edge1]
  diameter = 4
  invert = false
  length = 4
  lengthCustom = 12
  matchOuter = true
  offset = 0
  thread = false
  type = 33
FEATURE [Part::FeaturePython] Screw077  label="M3x12-Screw004"  # Fasteners workbench fastener (typed FeaturePython)
  Placement = pos=(41.25,-70.2,5e-15) rot=(-1,0,0;1.5708rad)
  baseObject = -> Washer036 [Edge1]
  diameter = 4
  invert = false
  length = 4
  lengthCustom = 12
  matchOuter = true
  offset = 0
  thread = false
  type = 33
FEATURE [Part::FeaturePython] Screw078  label="M3x12-Screw005"  # Fasteners workbench fastener (typed FeaturePython)
  Placement = pos=(70.2,-41.25,5e-15) rot=(0,-1,0;1.5708rad)
  baseObject = -> Washer035 [Edge1]
  diameter = 4
  invert = false
  length = 4
  lengthCustom = 12
  matchOuter = true
  offset = 0
  thread = false
  type = 33
FEATURE [Part::FeaturePython] Screw079  label="M3x12-Screw006"  # Fasteners workbench fastener (typed FeaturePython)
  Placement = pos=(-70.2,-41.25,5e-15) rot=(0,1,0;1.5708rad)
  baseObject = -> Washer042 [Edge1]
  diameter = 4
  invert = false
  length = 4
  lengthCustom = 12
  matchOuter = true
  offset = 0
  thread = false
  type = 33
FEATURE [Part::FeaturePython] Screw080  label="M3x12-Screw007"  # Fasteners workbench fastener (typed FeaturePython)
  Placement = pos=(-41.25,-70.2,5e-15) rot=(-1,0,0;1.5708rad)
  baseObject = -> Washer041 [Edge1]
  diameter = 4
  invert = false
  length = 4
  lengthCustom = 12
  matchOuter = true
  offset = 0
  thread = false
  type = 33
FEATURE [Part::FeaturePython] Screw081  label="M3x20-Screw007"  # Fasteners workbench fastener (typed FeaturePython)
  Placement = pos=(-41.25,-41.25,-8) rot=(1,0,0;3.14159rad)
  baseObject = -> Fillet001003 [Edge88]
  diameter = 1
  invert = false
  length = 6
  lengthCustom = 20
  matchOuter = true
  offset = 16
  thread = false
  type = 39
FEATURE [Part::FeaturePython] Screw082  label="M3x20-Screw008"  # Fasteners workbench fastener (typed FeaturePython)
  Placement = pos=(-41.25,41.25,-8) rot=(1,0,0;3.14159rad)
  baseObject = -> Fillet001002 [Edge88]
  diameter = 1
  invert = false
  length = 6
  lengthCustom = 20
  matchOuter = true
  offset = 16
  thread = false
  type = 39
FEATURE [Part::FeaturePython] Screw083  label="M3x20-Screw009"  # Fasteners workbench fastener (typed FeaturePython)
  Placement = pos=(41.25,41.25,-8) rot=(1,0,0;3.14159rad)
  baseObject = -> Fillet001001 [Edge88]
  diameter = 1
  invert = false
  length = 6
  lengthCustom = 20
  matchOuter = true
  offset = 16
  thread = false
  type = 39
FEATURE [Part::FeaturePython] Screw084  label="M3x20-Screw010"  # Fasteners workbench fastener (typed FeaturePython)
  Placement = pos=(41.25,-41.25,-8) rot=(1,0,0;3.14159rad)
  baseObject = -> Fillet001004 [Edge88]
  diameter = 1
  invert = false
  length = 6
  lengthCustom = 20
  matchOuter = true
  offset = 16
  thread = false
  type = 39
FEATURE [Part::Feature] Fusion001003002001001
  Placement = pos=(-85,-97,2.2e-14) rot=(-1,0,0;1.5708rad)
  shape: bbox 20 x 10 x 20 mm, 335 faces (baked)
FEATURE [Part::Feature] Fusion001003003001001
  Placement = pos=(55,-97,1e-15) rot=(-1,0,0;1.5708rad)
  shape: bbox 20 x 10 x 20 mm, 335 faces (baked)
FEATURE [Part::Feature] Fusion004025012001003
  Placement = pos=(-55,97,4e-14) rot=(0,0.707107,-0.707107;3.14159rad)
  shape: bbox 20 x 10 x 20 mm, 335 faces (baked)
FEATURE [Part::Feature] Fusion004025012001004
  Placement = pos=(85,97,6.5e-14) rot=(0,0.707107,-0.707107;3.14159rad)
  shape: bbox 20 x 10 x 20 mm, 335 faces (baked)
FEATURE [Part::Feature] Part__Mirroring002  label="bed-connector-mount"
  Placement = pos=(-9e-15,75,-10) rot=(0,1,0;3.14159rad)
  shape: bbox 116 x 22.25 x 12.2 mm, 268 faces (baked)
FEATURE [Part::FeaturePython] Screw087  label="M3x8-Screw006"  # Fasteners workbench fastener (typed FeaturePython)
  Placement = pos=(-10,85,-12.5) rot=(1,0,0;3.14159rad)
  baseObject = -> Part__Mirroring002 [Edge262]
  diameter = 1
  invert = true
  length = 1
  lengthCustom = 8
  matchOuter = true
  offset = 0
  thread = false
  type = 39
FEATURE [Part::FeaturePython] Washer043  label="M3-Washer070"  # Fasteners workbench fastener (typed FeaturePython)
  Placement = pos=(-54,85,-12.5) rot=(1,0,0;3.14159rad)
  baseObject = -> Part__Mirroring002 [Edge245]
  diameter = 4
  invert = true
  matchOuter = true
  offset = 0
  type = 5
FEATURE [Part::FeaturePython] Washer044  label="M3-Washer071"  # Fasteners workbench fastener (typed FeaturePython)
  Placement = pos=(54,85,-12.5) rot=(1,0,0;3.14159rad)
  baseObject = -> Part__Mirroring002 [Edge37]
  diameter = 4
  invert = true
  matchOuter = true
  offset = 0
  type = 5
FEATURE [Part::FeaturePython] Screw088  label="M3x8-Screw007"  # Fasteners workbench fastener (typed FeaturePython)
  Placement = pos=(-54,85,-13.05) rot=(1,0,0;3.14159rad)
  baseObject = -> Washer043 [Edge1]
  diameter = 4
  invert = false
  length = 2
  lengthCustom = 8
  matchOuter = true
  offset = 0
  thread = false
  type = 33
FEATURE [Part::FeaturePython] Screw089  label="M3x8-Screw008"  # Fasteners workbench fastener (typed FeaturePython)
  Placement = pos=(54,85,-13.05) rot=(1,0,0;3.14159rad)
  baseObject = -> Washer044 [Edge1]
  diameter = 4
  invert = false
  length = 2
  lengthCustom = 8
  matchOuter = true
  offset = 0
  thread = false
  type = 33
FEATURE [Part::Feature] Cut001001001
  Placement = pos=(0,103,9) rot=(1,0,0;3.14159rad)
  shape: bbox 30 x 9 x 18 mm, 48 faces (baked)
FEATURE [Part::Feature] Part__Feature075  label="221-412 v1 (5)"
  Placement = pos=(4.64965,94.325,-11.9983) rot=(-0.57735,0.57735,-0.57735;2.0944rad)
  shape: bbox 13.01 x 18.61 x 8.162 mm, 108 faces (baked)
FEATURE [Part::Feature] Part__Feature076  label="221-412 v1 (5)001"
  Placement = pos=(19.7497,94.325,-11.9983) rot=(-0.57735,0.57735,-0.57735;2.0944rad)
  shape: bbox 13.01 x 18.61 x 8.162 mm, 108 faces (baked)
FEATURE [Part::Feature] Part__Feature077  label="221-412 v1 (5)002"
  Placement = pos=(34.9497,94.325,-11.9983) rot=(-0.57735,0.57735,-0.57735;2.0944rad)
  shape: bbox 13.01 x 18.61 x 8.162 mm, 108 faces (baked)
FEATURE [Part::FeaturePython] Screw090  label="M3x10-Screw049"  # Fasteners workbench fastener (typed FeaturePython)
  Placement = pos=(-10,100,0) rot=(-1,0,0;1.5708rad)
  baseObject = -> Cut001001001 [Edge115]
  diameter = 4
  invert = true
  length = 3
  lengthCustom = 10
  matchOuter = true
  offset = 0
  thread = false
  type = 33
FEATURE [Part::FeaturePython] Screw091  label="M3x10-Screw050"  # Fasteners workbench fastener (typed FeaturePython)
  Placement = pos=(10,100,0) rot=(-1,0,0;1.5708rad)
  baseObject = -> Cut001001001 [Edge22]
  diameter = 4
  invert = true
  length = 3
  lengthCustom = 10
  matchOuter = true
  offset = 0
  thread = false
  type = 33
FEATURE [Part::Feature] Chamfer007003002006001
  Placement = pos=(-85,38,-10) rot=(0,1,0;3.14159rad)
  shape: bbox 18 x 36 x 7 mm, 142 faces (baked)
FEATURE [Part::FeaturePython] Screw092  label="M3x8-Screw009"  # Fasteners workbench fastener (typed FeaturePython)
  Placement = pos=(-85,45.5,-13) rot=(1,0,0;3.14159rad)
  baseObject = -> Chamfer007003002006001 [Edge356]
  diameter = 1
  invert = false
  length = 1
  lengthCustom = 8
  matchOuter = true
  offset = 0
  thread = false
  type = 39
FEATURE [Part::FeaturePython] Screw093  label="M3x8-Screw010"  # Fasteners workbench fastener (typed FeaturePython)
  Placement = pos=(-85,66.5,-13) rot=(1,0,0;3.14159rad)
  baseObject = -> Chamfer007003002006001 [Edge357]
  diameter = 1
  invert = false
  length = 1
  lengthCustom = 8
  matchOuter = true
  offset = 0
  thread = false
  type = 39
FEATURE [Part::Feature] Cut011001
  Placement = pos=(-77,85,-10) rot=(0.707107,0.707107,0;3.14159rad)
  shape: bbox 36 x 20 x 6 mm, 59 faces (baked)
FEATURE [Part::Cylinder] Cylinder  label="6x16-dowel-pin-001"
  Angle = 360
  AttacherType = Attacher::AttachEngine3D
  Height = 16
  Placement = pos=(-125,-77,-20) rot=(1,0,0;1.5708rad)
  Radius = 3
FEATURE [Part::Cylinder] Cylinder001  label="6x16-dowel-pin-002"
  Angle = 360
  AttacherType = Attacher::AttachEngine3D
  Height = 16
  Placement = pos=(-115,-77,-20) rot=(1,0,0;1.5708rad)
  Radius = 3
FEATURE [Part::Cylinder] Cylinder002  label="6x16-dowel-pin-003"
  Angle = 360
  AttacherType = Attacher::AttachEngine3D
  Height = 16
  Placement = pos=(-115,93,-20) rot=(1,0,0;1.5708rad)
  Radius = 3
FEATURE [Part::Cylinder] Cylinder003  label="6x16-dowel-pin-004"
  Angle = 360
  AttacherType = Attacher::AttachEngine3D
  Height = 16
  Placement = pos=(-125,93,-20) rot=(1,0,0;1.5708rad)
  Radius = 3
FEATURE [Part::Cylinder] Cylinder004  label="6x16-dowel-pin-005"
  Angle = 360
  AttacherType = Attacher::AttachEngine3D
  Height = 16
  Placement = pos=(128,5,-20) rot=(0.57735,-0.57735,-0.57735;2.0944rad)
  Radius = 3
FEATURE [Part::Cylinder] Cylinder005  label="6x16-dowel-pin-006"
  Angle = 360
  AttacherType = Attacher::AttachEngine3D
  Height = 16
  Placement = pos=(128,-5,-20) rot=(0.57735,-0.57735,-0.57735;2.0944rad)
  Radius = 3
FEATURE [Part::FeaturePython] Screw094  label="M3x25-Screw"  # Fasteners workbench fastener (typed FeaturePython)
  Placement = pos=(-138.7,85,-25.5) rot=(0,-1,0;1.5708rad)
  diameter = 4
  invert = true
  length = 8
  lengthCustom = 25
  matchOuter = true
  offset = 0
  thread = false
  type = 33
FEATURE [Part::FeaturePython] Screw095  label="M3x25-Screw003"  # Fasteners workbench fastener (typed FeaturePython)
  Placement = pos=(-138.7,-85,-25.5) rot=(0,-1,0;1.5708rad)
  diameter = 4
  invert = true
  length = 8
  lengthCustom = 25
  matchOuter = true
  offset = 0
  thread = false
  type = 33
FEATURE [Part::FeaturePython] Screw096  label="M3x25-Screw004"  # Fasteners workbench fastener (typed FeaturePython)
  Placement = pos=(138.7,0,-25.5) rot=(0,1,0;1.5708rad)
  diameter = 4
  invert = false
  length = 8
  lengthCustom = 25
  matchOuter = true
  offset = 0
  thread = false
  type = 33
FEATURE [Part::Feature] Chamfer001001001  label="bottom-spring-spacer-001"
  Placement = pos=(-120,-100,-30.5) rot=(-1,0,0;1.5708rad)
  shape: bbox 7 x 10.5 x 7 mm, 14 faces (baked)
FEATURE [Part::Feature] Chamfer004013007011015006009007001005003007001003  label="bottom-spring-spacer-002"
  Placement = pos=(-120,-70,-30.5) rot=(0,0.707107,-0.707107;3.14159rad)
  shape: bbox 7 x 10.5 x 7 mm, 14 faces (baked)
FEATURE [Part::Feature] Chamfer004013007011015006009007001005003007001004  label="bottom-spring-spacer-003"
  Placement = pos=(-120,100,-30.5) rot=(0,0.707107,-0.707107;3.14159rad)
  shape: bbox 7 x 10.5 x 7 mm, 14 faces (baked)
FEATURE [Part::Feature] Chamfer004013007011015006009007001005003007001005  label="bottom-spring-spacer-004"
  Placement = pos=(-120,70,-30.5) rot=(-1,0,0;1.5708rad)
  shape: bbox 7 x 10.5 x 7 mm, 14 faces (baked)
FEATURE [Part::Feature] Chamfer004013007011015006009007001005003007001006  label="bottom-spring-spacer-005"
  Placement = pos=(120,-15,-30.5) rot=(-1,0,0;1.5708rad)
  shape: bbox 7 x 10.5 x 7 mm, 14 faces (baked)
FEATURE [Part::Feature] Chamfer004013007011015006009007001005003007001007  label="bottom-spring-spacer-006"
  Placement = pos=(120,15,-30.5) rot=(0,0.707107,-0.707107;3.14159rad)
  shape: bbox 7 x 10.5 x 7 mm, 14 faces (baked)
FEATURE [Part::Feature] Chamfer002001001  label="top-spring-spacer-001"
  Placement = pos=(-117,-100,-4) rot=(0,0.707107,0.707107;3.14159rad)
  shape: bbox 7 x 7 x 7 mm, 14 faces (baked)
FEATURE [Part::Feature] Chamfer004013007011015006009007001005003007001008  label="top-spring-spacer-002"
  Placement = pos=(-117,-70,-4) rot=(1,0,0;1.5708rad)
  shape: bbox 7 x 7 x 7 mm, 14 faces (baked)
FEATURE [Part::Feature] Chamfer004013007011015006009007001005003007001009  label="top-spring-spacer-003"
  Placement = pos=(-117,100,-4) rot=(1,0,0;1.5708rad)
  shape: bbox 7 x 7 x 7 mm, 14 faces (baked)
FEATURE [Part::Feature] Chamfer004013007011015006009007001005003007001010  label="top-spring-spacer-004"
  Placement = pos=(-117,70,-4) rot=(0,0.707107,0.707107;3.14159rad)
  shape: bbox 7 x 7 x 7 mm, 14 faces (baked)
FEATURE [Part::Feature] Chamfer004013007011015006009007001005003007001011  label="top-spring-spacer-005"
  Placement = pos=(117,-15,-4) rot=(0,0.707107,0.707107;3.14159rad)
  shape: bbox 7 x 7 x 7 mm, 14 faces (baked)
FEATURE [Part::Feature] Chamfer004013007011015006009007001005003007001012  label="top-spring-spacer-006"
  Placement = pos=(117,15,-4) rot=(1,0,0;1.5708rad)
  shape: bbox 7 x 7 x 7 mm, 14 faces (baked)
FEATURE [Part::Feature] Body001001001  label="hook-spring-001"
  Placement = pos=(-119.5,-101,-27.5) rot=(0,0,1;0rad)
  shape: bbox 6.31 x 4.635 x 20.83 mm, 22 faces (baked)
FEATURE [Part::Feature] Body001001002  label="hook-spring-002"
  Placement = pos=(-119.5,-69,-27.5) rot=(0,0,1;0rad)
  shape: bbox 6.31 x 4.635 x 20.83 mm, 22 faces (baked)
FEATURE [Part::Feature] Body001001003  label="hook-spring-003"
  Placement = pos=(-119.5,69,-27.5) rot=(0,0,1;0rad)
  shape: bbox 6.31 x 4.635 x 20.83 mm, 22 faces (baked)
FEATURE [Part::Feature] Body001001004  label="hook-spring-004"
  Placement = pos=(-119.5,101,-27.5) rot=(0,0,1;0rad)
  shape: bbox 6.31 x 4.635 x 20.83 mm, 22 faces (baked)
FEATURE [Part::Feature] Body001001005  label="hook-spring-005"
  Placement = pos=(119,-16,-27.5) rot=(0,0,1;0rad)
  shape: bbox 6.31 x 4.635 x 20.83 mm, 22 faces (baked)
FEATURE [Part::Feature] Body001001006  label="hook-spring-006"
  Placement = pos=(119,16,-27.5) rot=(0,0,1;0rad)
  shape: bbox 6.31 x 4.635 x 20.83 mm, 22 faces (baked)
FEATURE [Part::Feature] Fusion004025023015005001003  label="y-slider-r1-f4-limit004"
  Placement = pos=(-142,-85,-42.5) rot=(0,0,1;0rad)
  shape: bbox 45 x 37.5 x 48.4 mm, 125 faces (baked)
FEATURE [Part::Feature] Fusion004025023015005001004  label="y-slider-r1-f4-limit005"
  Placement = pos=(-142,85,-42.5) rot=(0,0,1;0rad)
  shape: bbox 45 x 37.5 x 48.4 mm, 125 faces (baked)
FEATURE [Part::Feature] Part__Mirroring001002002001  label="x-slider-r1-f4-limit001 (Mirror #2)001"
  Placement = pos=(142,0,-42.5) rot=(0,0,1;0rad)
  shape: bbox 45 x 37.5 x 48.4 mm, 115 faces (baked)
FEATURE [App::Part] Part007  label="bed-assembly"
  Group = -> [Box001,AdditivePipe001,AdditivePipe003,AdditivePipe005,Part005,Part006,Cut010,Solid,Screw001,Screw,Solid001,Screw003,Screw002,Solid002,Screw005,Screw004,Screw007,Solid003,Screw006,Screw013,Screw012,Screw011,Screw040,Screw039,Screw042,Washer013,Washer011,Washer012,Screw041,Washer010,Washer017,Washer016,Screw037,Screw036,Screw035,Washer015,Screw034,Washer014,Washer020,Screw046,Screw043,Screw044,+125 more]
  Origin = -> Origin007
